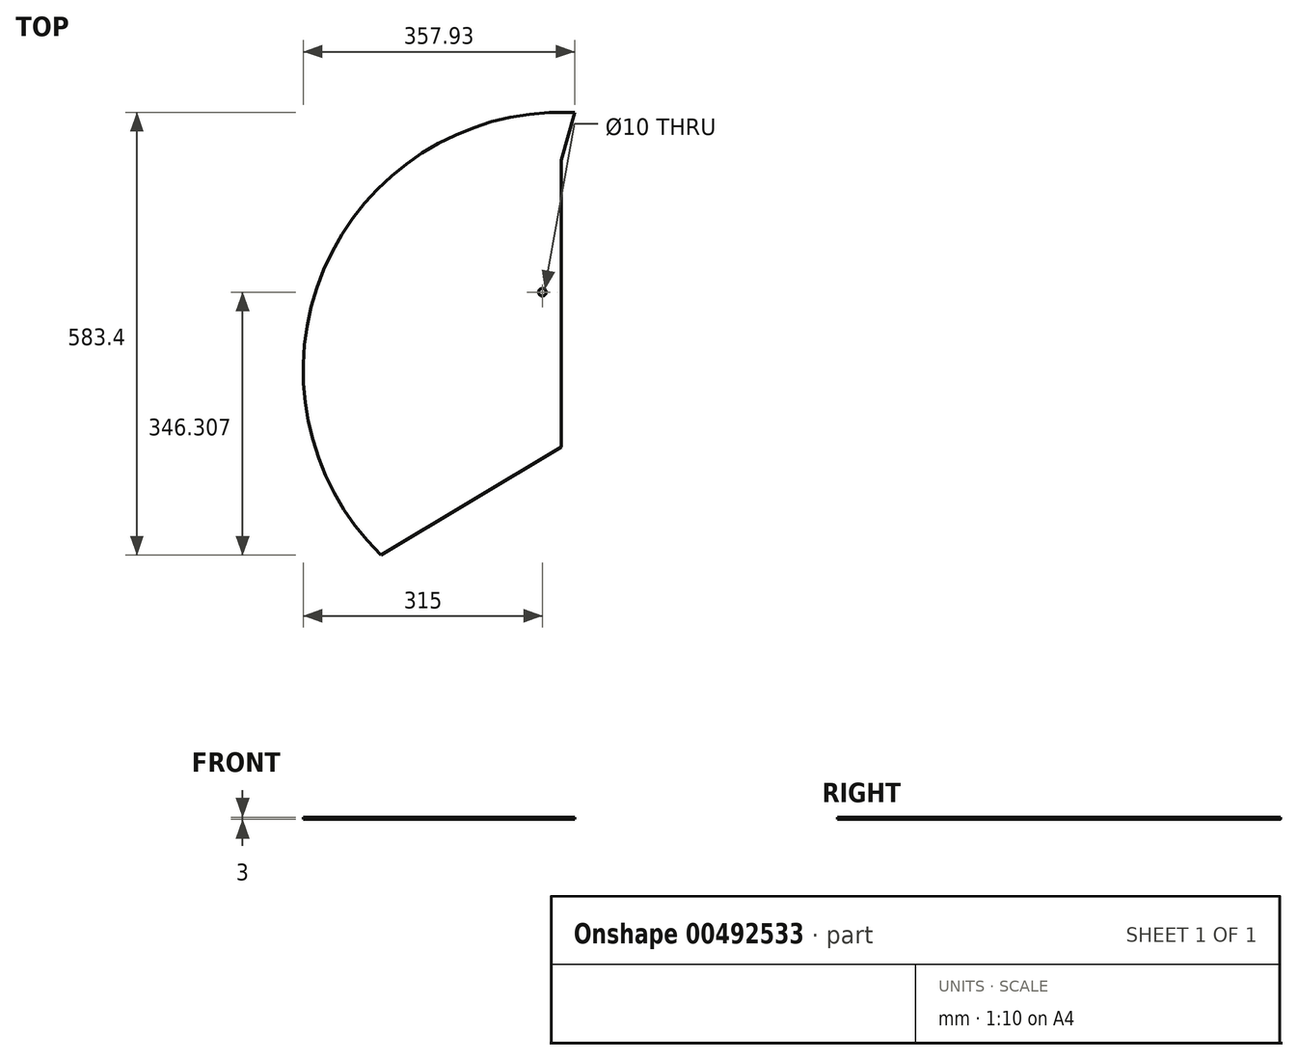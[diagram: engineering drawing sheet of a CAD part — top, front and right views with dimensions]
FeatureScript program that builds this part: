
annotation { "Feature Type Name" : "Feature", "Feature Type Description" : "" }
export const myFeature = defineFeature(function(context is Context, id is Id, definition is map)
    precondition{}
    {
        {
            var Q0;
            Q0=qCreatedBy(makeId("Top.planeOp"),FACE);
            var sketch = newSketch(context, id + "F0", { "sketchPlane" : qUnion([Q0])});
            skArc(sketch, "E0", {"start": v(34.93, 476.63) * mm, "mid": v(-288.02, 269.5) * mm, "end": v(-212.4, -106.63) * mm});
            skLineSegment(sketch, "E1", {"start": v(25, 136.77) * mm, "end": v(25, 413.91) * mm});
            skLineSegment(sketch, "E2", {"start": v(25, 136.77) * mm, "end": v(25, 35.8) * mm});
            skLineSegment(sketch, "E3", {"start": v(-212.4, -106.63) * mm, "end": v(25, 35.8) * mm});
            skLineSegment(sketch, "E4", {"start": v(34.93, 476.63) * mm, "end": v(42.93, 476.4) * mm});
            skLineSegment(sketch, "E5", {"start": v(42.93, 476.4) * mm, "end": v(25, 413.91) * mm});
            skCircle(sketch, "E6", {"center": v(0, 239.68) * mm, "radius": 5 * mm});
            skSolve(sketch);
        }
        {
            var Q0;
            Q0=qSketchRegion(id+"F0",true);
            extrude(context, id + "F1", {"entities" : qUnion([Q0]), "offsetDistance" : 25 * mm, "depth" : 3 * mm});
        }
        {
            var Q0;
            Q0 = qSketchRegion(id + "F0", true);
            extrude(context, id + "F2", {"entities" : qUnion([Q0]), "operationType" : NewBodyOperationType.ADD, "depth" : 3 * mm, "offsetDistance" : 25 * mm});
        }
    });
